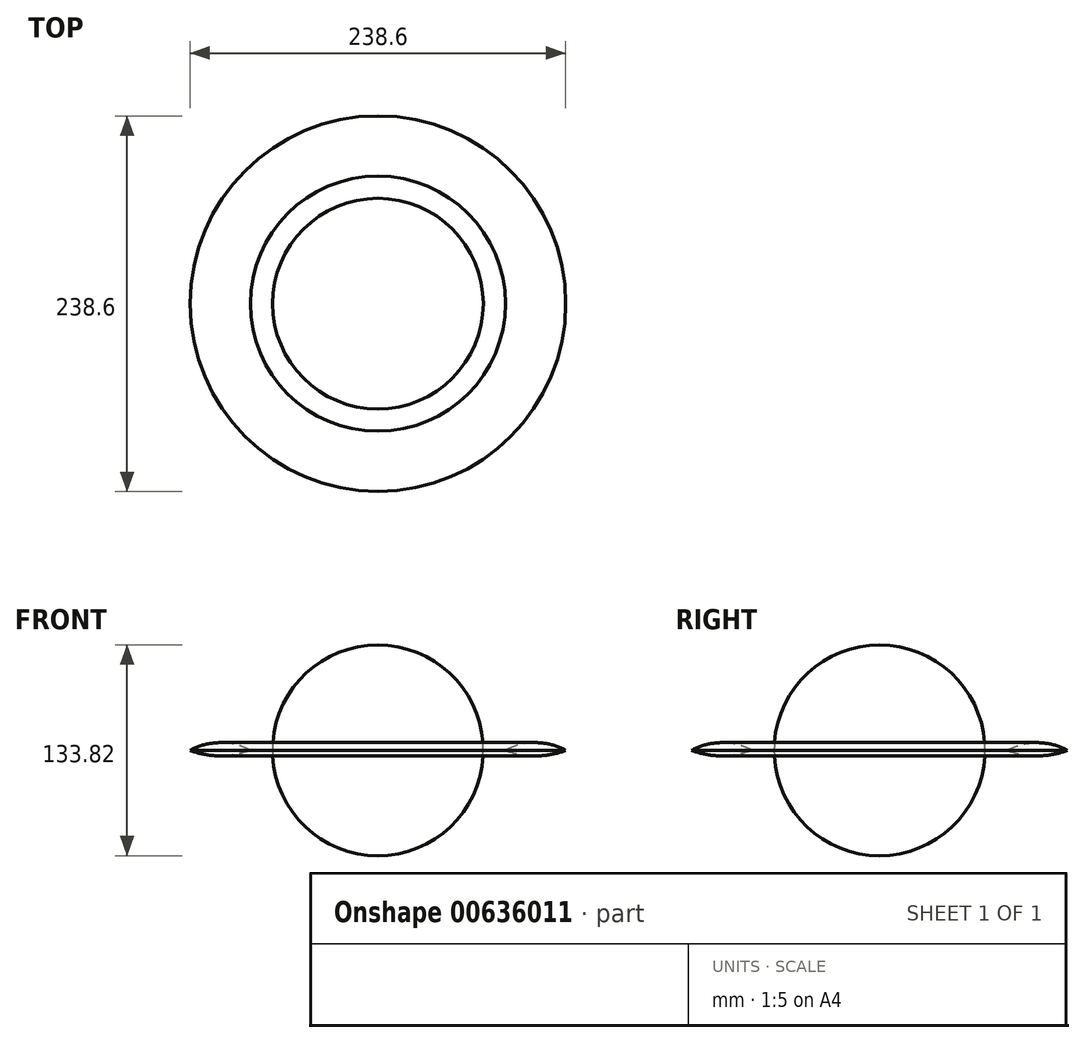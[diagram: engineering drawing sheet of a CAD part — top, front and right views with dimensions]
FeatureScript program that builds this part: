
annotation { "Feature Type Name" : "Feature", "Feature Type Description" : "" }
export const myFeature = defineFeature(function(context is Context, id is Id, definition is map)
    precondition{}
    {
        {
            var Q0;
            Q0=qCreatedBy(makeId("Front.planeOp"),FACE);
            var sketch = newSketch(context, id + "F0", { "sketchPlane" : qUnion([Q0])});
            skArc(sketch, "E0", {"start": v(0, 66.91) * mm, "mid": v(-66.91, 0) * mm, "end": v(0, -66.91) * mm});
            skLineSegment(sketch, "E1", {"start": v(0, 66.91) * mm, "end": v(0, -66.91) * mm});
            skSolve(sketch);
        }
        {
            var Q0;
            Q0=makeQuery(id+"F0.imprint","IMPRINT",FACE,{"disambiguationData":[TD([[makeQuery(id+"F0.imprint","IMPRINT",EDGE,{"derivedFrom":sQuery(id+"F0.wireOp",EDGE,"E0")}),1.0]])]});
            var Q1;
            Q1=sQuery(id+"F0.wireOp",EDGE,"E1");
            revolve(context, id + "F1", {"entities" : qUnion([Q0]), "axis" : qUnion([Q1]), "revolveType" : RevolveType.FULL});
        }
        {
            var Q0;
            Q0=qCreatedBy(makeId("Front.planeOp"),FACE);
            var sketch = newSketch(context, id + "F2", { "sketchPlane" : qUnion([Q0])});
            skLineSegment(sketch, "E2", {"start": v(-81.02, 0) * mm, "end": v(-119.3, 0) * mm});
            skArc(sketch, "E3", {"start": v(-81.02, 0) * mm, "mid": v(-100.16, 4.88) * mm, "end": v(-119.3, 0) * mm});
            skArc(sketch, "E4", {"start": v(-119.3, 0) * mm, "mid": v(-100.16, -3.55) * mm, "end": v(-81.02, 0) * mm});
            skSolve(sketch);
        }
        {
            var Q0;
            Q0=makeQuery(id+"F2.imprint","IMPRINT",FACE,{"disambiguationData":[TD([[makeQuery(id+"F2.imprint","IMPRINT",EDGE,{"derivedFrom":sQuery(id+"F2.wireOp",EDGE,"E2")}),-1.0]])]});
            var Q1;
            Q1=makeQuery(id+"F2.imprint","IMPRINT",FACE,{"disambiguationData":[TD([[makeQuery(id+"F2.imprint","IMPRINT",EDGE,{"derivedFrom":sQuery(id+"F2.wireOp",EDGE,"E2")}),1.0]])]});
            var Q2;
            Q2=sQuery(id+"F0.wireOp",EDGE,"E1");
            revolve(context, id + "F3", {"entities" : qUnion([Q0, Q1]), "axis" : qUnion([Q2]), "revolveType" : RevolveType.FULL});
        }
    });
